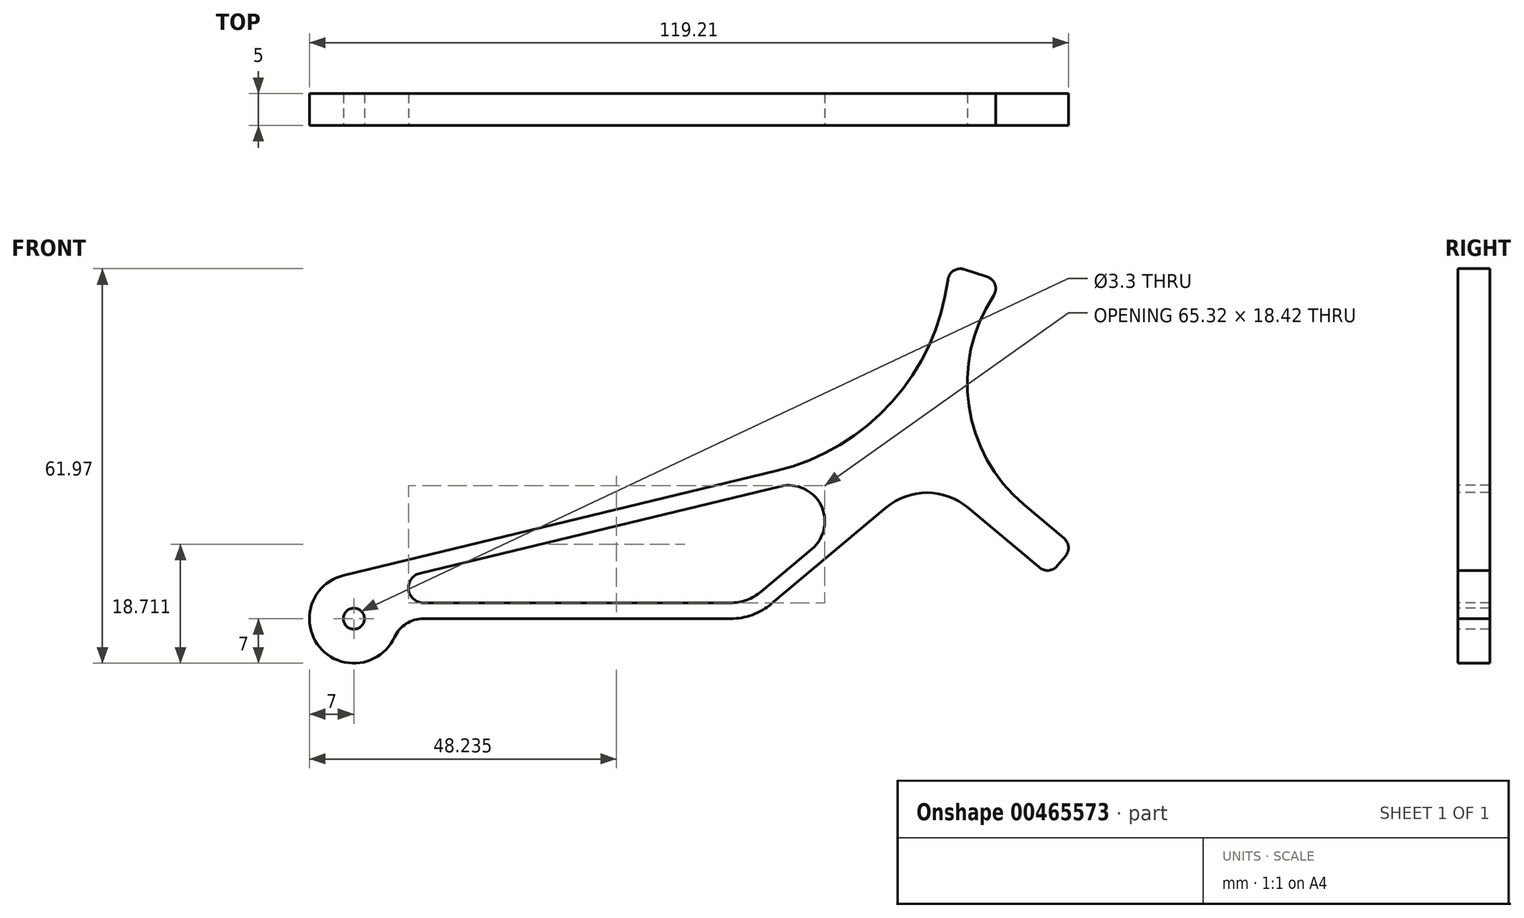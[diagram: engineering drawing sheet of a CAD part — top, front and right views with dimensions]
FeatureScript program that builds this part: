
annotation { "Feature Type Name" : "Feature", "Feature Type Description" : "" }
export const myFeature = defineFeature(function(context is Context, id is Id, definition is map)
    precondition{}
    {
        {
            var Q0;
            Q0=qCreatedBy(makeId("Front.planeOp"),FACE);
            var sketch = newSketch(context, id + "F0", { "sketchPlane" : qUnion([Q0])});
            skCircle(sketch, "E0", {"center": v(0, 0) * mm, "radius": 17.5 * mm, "construction": true});
            skArc(sketch, "E1", {"start": v(-91.64, 6.8) * mm, "mid": v(-95.4, -4.45) * mm, "end": v(-83.64, -2.92) * mm});
            skLineSegment(sketch, "E2", {"start": v(-30.86, 0) * mm, "end": v(-79.1, 0) * mm});
            skPoint(sketch, "E3.visualSharp", {"position": v(-83, 0) * mm});
            skArc(sketch, "E3.filletArc", {"start": v(-79.1, 0) * mm, "mid": v(-81.8, -0.8) * mm, "end": v(-83.64, -2.92) * mm});
            skLineSegment(sketch, "E4", {"start": v(-24.44, 2.34) * mm, "end": v(-6.43, 17.45) * mm});
            skLineSegment(sketch, "E5", {"start": v(6.43, 17.45) * mm, "end": v(17.64, 8.05) * mm});
            skLineSegment(sketch, "E6", {"start": v(-91.64, 6.8) * mm, "end": v(-23.65, 23.22) * mm});
            skPoint(sketch, "E7.orphan", {"position": v(-17.5, 0) * mm});
            skPoint(sketch, "E8.visualSharp", {"position": v(0, 22.84) * mm});
            skArc(sketch, "E8.filletArc", {"start": v(6.43, 17.45) * mm, "mid": v(0, 19.8) * mm, "end": v(-6.43, 17.45) * mm});
            skPoint(sketch, "E9.visualSharp", {"position": v(-27.23, 0) * mm});
            skArc(sketch, "E9.filletArc", {"start": v(-30.86, 0) * mm, "mid": v(-27.44, 0.6) * mm, "end": v(-24.44, 2.34) * mm});
            skLineSegment(sketch, "E10", {"start": v(21.74, 9.82) * mm, "end": v(20.46, 8.3) * mm});
            skArc(sketch, "E11", {"start": v(-23.65, 23.22) * mm, "mid": v(-5.53, 34.04) * mm, "end": v(3.27, 53.22) * mm});
            skLineSegment(sketch, "E12", {"start": v(5.86, 54.87) * mm, "end": v(9.38, 53.75) * mm});
            skArc(sketch, "E13", {"start": v(10.44, 50.74) * mm, "mid": v(6.58, 33.41) * mm, "end": v(15.22, 17.9) * mm});
            skArc(sketch, "E14.filletArc", {"start": v(17.64, 8.05) * mm, "mid": v(19.1, 7.58) * mm, "end": v(20.46, 8.3) * mm});
            skLineSegment(sketch, "E15", {"start": v(15.22, 17.9) * mm, "end": v(21.5, 12.64) * mm});
            skArc(sketch, "E16.filletArc", {"start": v(21.74, 9.82) * mm, "mid": v(22.2, 11.28) * mm, "end": v(21.5, 12.64) * mm});
            skPoint(sketch, "E17.visualSharp", {"position": v(3.5, 55.63) * mm});
            skArc(sketch, "E17.filletArc", {"start": v(5.86, 54.87) * mm, "mid": v(4.18, 54.66) * mm, "end": v(3.27, 53.22) * mm});
            skPoint(sketch, "E18.visualSharp", {"position": v(12.04, 52.9) * mm});
            skArc(sketch, "E18.filletArc", {"start": v(10.44, 50.74) * mm, "mid": v(10.66, 52.51) * mm, "end": v(9.38, 53.75) * mm});
            skLineSegment(sketch, "E19.0", {"start": v(-30.86, 2.5) * mm, "end": v(-79.1, 2.5) * mm});
            skArc(sketch, "E19.1", {"start": v(-30.86, 2.5) * mm, "mid": v(-28.3, 2.95) * mm, "end": v(-26.04, 4.25) * mm});
            skLineSegment(sketch, "E19.2", {"start": v(-26.04, 4.25) * mm, "end": v(-18.08, 10.93) * mm});
            skLineSegment(sketch, "E20", {"start": v(-79.64, 7.13) * mm, "end": v(-23.06, 20.8) * mm});
            skArc(sketch, "E21", {"start": v(-18.08, 10.93) * mm, "mid": v(-16.67, 17.83) * mm, "end": v(-23.06, 20.8) * mm});
            skLineSegment(sketch, "E22", {"start": v(-23.65, 23.22) * mm, "end": v(-23.06, 20.8) * mm, "construction": true});
            skArc(sketch, "E23", {"start": v(-79.64, 7.13) * mm, "mid": v(-81.42, 4.57) * mm, "end": v(-79.1, 2.5) * mm});
            skSolve(sketch);
        }
        {
            var Q0;
            Q0=makeQuery(id+"F0.imprint","IMPRINT",FACE,{"disambiguationData":[TD([[makeQuery(id+"F0.imprint","IMPRINT",EDGE,{"derivedFrom":sQuery(id+"F0.wireOp",EDGE,"E1")}),1.0]])]});
            extrude(context, id + "F1", {"entities" : qUnion([Q0]), "oppositeDirection" : true, "depth" : 5 * mm});
        }
        {
            var Q0;
            Q0=makeQuery(id+"F1.opExtrude","CAP_FACE",FACE,{"disambiguationData":[OSD([sQuery(id+"F0.wireOp",EDGE,"E1"),sQuery(id+"F0.wireOp",EDGE,"E2"),sQuery(id+"F0.wireOp",EDGE,"E3.filletArc"),sQuery(id+"F0.wireOp",EDGE,"E4"),sQuery(id+"F0.wireOp",EDGE,"E5"),sQuery(id+"F0.wireOp",EDGE,"E6"),sQuery(id+"F0.wireOp",EDGE,"E8.filletArc"),sQuery(id+"F0.wireOp",EDGE,"E9.filletArc"),sQuery(id+"F0.wireOp",EDGE,"E10"),sQuery(id+"F0.wireOp",EDGE,"E11"),sQuery(id+"F0.wireOp",EDGE,"E12"),sQuery(id+"F0.wireOp",EDGE,"E13"),sQuery(id+"F0.wireOp",EDGE,"E14.filletArc"),sQuery(id+"F0.wireOp",EDGE,"E15"),sQuery(id+"F0.wireOp",EDGE,"E16.filletArc"),sQuery(id+"F0.wireOp",EDGE,"E17.filletArc"),sQuery(id+"F0.wireOp",EDGE,"E18.filletArc"),sQuery(id+"F0.wireOp",EDGE,"E19.0"),sQuery(id+"F0.wireOp",EDGE,"E19.1"),sQuery(id+"F0.wireOp",EDGE,"E19.2"),sQuery(id+"F0.wireOp",EDGE,"E20"),sQuery(id+"F0.wireOp",EDGE,"E21"),sQuery(id+"F0.wireOp",EDGE,"E23")])],"isStart":true});
            var sketch = newSketch(context, id + "F2", { "sketchPlane" : qUnion([Q0])});
            skPoint(sketch, "E24", {"position": v(-90, 0) * mm});
            skSolve(sketch);
        }
        {
            var Q0;
            Q0=sQuery(id+"F2.wireOp",VERTEX,"E24");
            var Q1;
            Q1=makeQuery(id+"F1.opExtrude","SWEPT_BODY",BODY,{"disambiguationData":[OSD([sQuery(id+"F0.wireOp",EDGE,"E1"),sQuery(id+"F0.wireOp",EDGE,"E2"),sQuery(id+"F0.wireOp",EDGE,"E3.filletArc"),sQuery(id+"F0.wireOp",EDGE,"E4"),sQuery(id+"F0.wireOp",EDGE,"E5"),sQuery(id+"F0.wireOp",EDGE,"E6"),sQuery(id+"F0.wireOp",EDGE,"E8.filletArc"),sQuery(id+"F0.wireOp",EDGE,"E9.filletArc"),sQuery(id+"F0.wireOp",EDGE,"E10"),sQuery(id+"F0.wireOp",EDGE,"E11"),sQuery(id+"F0.wireOp",EDGE,"E12"),sQuery(id+"F0.wireOp",EDGE,"E13"),sQuery(id+"F0.wireOp",EDGE,"E14.filletArc"),sQuery(id+"F0.wireOp",EDGE,"E15"),sQuery(id+"F0.wireOp",EDGE,"E16.filletArc"),sQuery(id+"F0.wireOp",EDGE,"E17.filletArc"),sQuery(id+"F0.wireOp",EDGE,"E18.filletArc"),sQuery(id+"F0.wireOp",EDGE,"E19.0"),sQuery(id+"F0.wireOp",EDGE,"E19.1"),sQuery(id+"F0.wireOp",EDGE,"E19.2"),sQuery(id+"F0.wireOp",EDGE,"E20"),sQuery(id+"F0.wireOp",EDGE,"E21"),sQuery(id+"F0.wireOp",EDGE,"E23")])]});
            hole(context, id + "F3", {"style" : HoleStyle.SIMPLE, "endStyle" : HoleEndStyle.THROUGH, "standardTappedOrClearance" : lookupTablePath({ "standard" : "ISO", "engagement" : "75%", "pitch" : "0.7 mm", "size" : "M4", "type" : "Tapped" }), "standardBlindInLast" : lookupTablePath({ "standard" : "ISO", "engagement" : "75%", "pitch" : "0.7 mm", "size" : "M4", "type" : "Tapped" }), "holeDiameter" : 3.3 * mm, "showTappedDepth" : true, "isTappedThrough" : true, "tappedDepth" : 12 * mm, "tapClearance" : 3, "locations" : qUnion([Q0]), "scope" : qUnion([Q1]), "majorDiameter" : 4 * mm});
        }
    });
